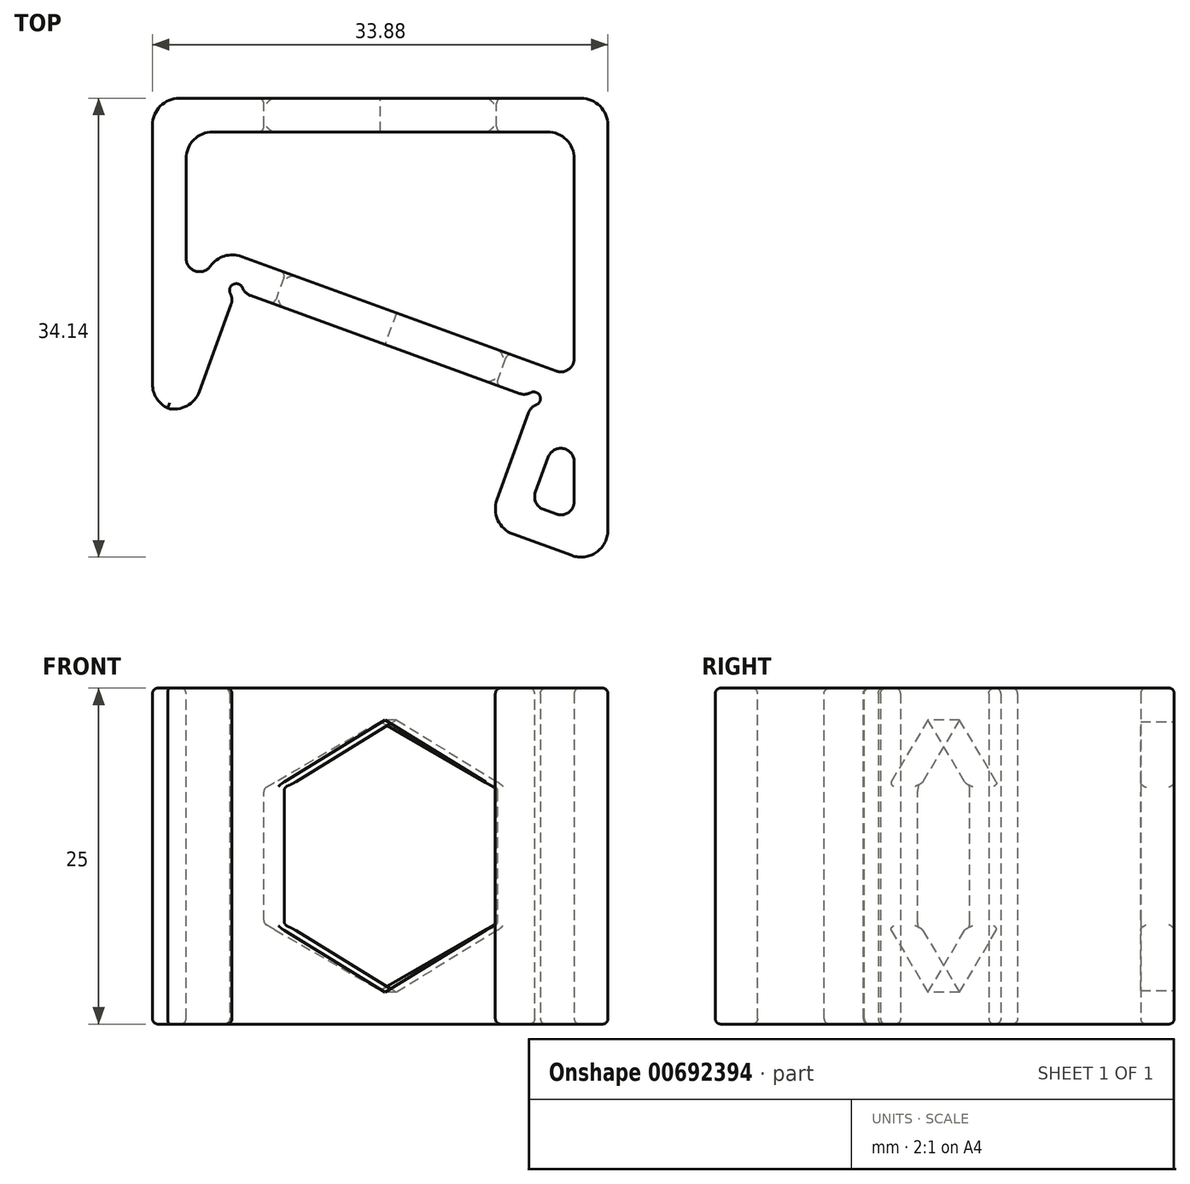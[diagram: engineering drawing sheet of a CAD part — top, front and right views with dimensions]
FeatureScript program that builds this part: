
annotation { "Feature Type Name" : "Feature", "Feature Type Description" : "" }
export const myFeature = defineFeature(function(context is Context, id is Id, definition is map)
    precondition{}
    {
        {
            var Q0;
            Q0=qCreatedBy(makeId("Right.planeOp"),FACE);
            var sketch = newSketch(context, id + "F0", { "sketchPlane" : qUnion([Q0])});
            skLineSegment(sketch, "E0", {"start": v(0, 0) * mm, "end": v(14.56, 0) * mm});
            skLineSegment(sketch, "E1", {"start": v(14.56, 0) * mm, "end": v(14.56, 40) * mm, "construction": true});
            skLineSegment(sketch, "E2", {"start": v(14.56, 40) * mm, "end": v(11.3, 31.06) * mm});
            skPoint(sketch, "E3", {"position": v(7.28, 20) * mm});
            skLineSegment(sketch, "E4", {"start": v(12.65, 5.51) * mm, "end": v(20.7, 27.64) * mm});
            skLineSegment(sketch, "E5", {"start": v(16.68, 16.58) * mm, "end": v(7.28, 20) * mm, "construction": true});
            skLineSegment(sketch, "E6", {"start": v(14.56, 0) * mm, "end": v(35, 0) * mm});
            skLineSegment(sketch, "E7", {"start": v(35, 0) * mm, "end": v(35, 40) * mm});
            skLineSegment(sketch, "E8", {"start": v(35, 40) * mm, "end": v(14.56, 40) * mm});
            skLineSegment(sketch, "E9", {"start": v(12.65, 5.51) * mm, "end": v(3.25, 8.94) * mm});
            skLineSegment(sketch, "E10", {"start": v(20.7, 27.64) * mm, "end": v(11.3, 31.06) * mm});
            skLineSegment(sketch, "E11", {"start": v(3.25, 8.94) * mm, "end": v(0, 0) * mm});
            skLineSegment(sketch, "E12", {"start": v(11.3, 31.06) * mm, "end": v(3.25, 8.94) * mm, "construction": true});
            skCircle(sketch, "E13", {"center": v(20.7, 27.64) * mm, "radius": 0.5 * mm});
            skCircle(sketch, "E14", {"center": v(12.65, 5.51) * mm, "radius": 0.5 * mm});
            skLineSegment(sketch, "E15", {"start": v(12.33, 33.88) * mm, "end": v(35, 33.88) * mm});
            skLineSegment(sketch, "E16.0", {"start": v(4.75, 5.73) * mm, "end": v(3.57, 2.5) * mm});
            skLineSegment(sketch, "E16.1", {"start": v(14.14, 2.31) * mm, "end": v(4.75, 5.73) * mm});
            skLineSegment(sketch, "E16.2", {"start": v(3.57, 2.5) * mm, "end": v(23.1, 2.5) * mm});
            skLineSegment(sketch, "E16.3", {"start": v(14.14, 2.31) * mm, "end": v(23.9, 29.14) * mm});
            skLineSegment(sketch, "E16.4", {"start": v(23.9, 29.14) * mm, "end": v(14.51, 32.56) * mm});
            skLineSegment(sketch, "E16.5", {"start": v(23.1, 2.5) * mm, "end": v(32.5, 2.5) * mm});
            skLineSegment(sketch, "E16.6", {"start": v(32.5, 2.5) * mm, "end": v(32.5, 37.5) * mm});
            skLineSegment(sketch, "E16.7", {"start": v(32.5, 37.5) * mm, "end": v(16.3, 37.5) * mm});
            skLineSegment(sketch, "E16.8", {"start": v(16.3, 37.5) * mm, "end": v(14.51, 32.56) * mm});
            skLineSegment(sketch, "E17", {"start": v(32.5, 31.38) * mm, "end": v(17.74, 31.38) * mm});
            skSolve(sketch);
        }
        {
            var Q0;
            Q0=makeQuery(id+"F0.imprint","IMPRINT",FACE,{"disambiguationData":[TD([[makeQuery(id+"F0.imprint","IMPRINT",EDGE,{"derivedFrom":sQuery(id+"F0.wireOp",EDGE,"E0")}),1.0]])]});
            var Q1;
            {var subQ0=sQuery(id+"F0.wireOp",EDGE,"E16.3");var subQ1=sQuery(id+"F0.wireOp",EDGE,"E16.1");var subQ2=makeQuery(id+"F0.imprint","INTERSECT",VERTEX,{"derivedFrom":[subQ1,subQ0]});Q1=makeQuery(id+"F0.imprint","IMPRINT",FACE,{"disambiguationData":[TD([[makeQuery(id+"F0.imprint","IMPRINT",EDGE,{"disambiguationData":[TD([[subQ2,-1.0]])],"derivedFrom":subQ1}),-1.0]])]});}
            var Q2;
            {var subQ5=sQuery(id+"F0.wireOp",EDGE,"E17");Q2=makeQuery(id+"F0.imprint","IMPRINT",FACE,{"disambiguationData":[TD([[makeQuery(id+"F0.imprint","IMPRINT",EDGE,{"derivedFrom":subQ5}),-1.0]])]});}
            extrude(context, id + "F1", {"entities" : qUnion([Q0, Q1, Q2]), "depth" : 25 * mm, "offsetDistance" : 25 * mm});
        }
        {
            var Q0;
            Q0=makeQuery(id+"F1.opExtrude","SWEPT_FACE",FACE,{"disambiguationData":[OSD([sQuery(id+"F0.wireOp",EDGE,"E4")])]});
            var sketch = newSketch(context, id + "F2", { "sketchPlane" : qUnion([Q0])});
            skPoint(sketch, "E18.0", {"position": v(12.5, 32.56) * mm});
            skPoint(sketch, "E18.1", {"position": v(0, 21.28) * mm});
            skLineSegment(sketch, "E19", {"start": v(0, 21.28) * mm, "end": v(22.76, 21.28) * mm, "construction": true});
            skLineSegment(sketch, "E20", {"start": v(12.5, 32.56) * mm, "end": v(12.5, 21.28) * mm, "construction": true});
            skCircle(sketch, "E21.cCircle", {"center": v(12.5, 21.28) * mm, "radius": 8.78 * mm, "construction": true});
            skLineSegment(sketch, "E21.0", {"start": v(7.43, 30.06) * mm, "end": v(17.57, 30.06) * mm});
            skLineSegment(sketch, "E21.1", {"start": v(17.57, 30.06) * mm, "end": v(22.63, 21.28) * mm});
            skLineSegment(sketch, "E21.2", {"start": v(22.63, 21.28) * mm, "end": v(17.57, 12.5) * mm});
            skLineSegment(sketch, "E21.3", {"start": v(17.57, 12.5) * mm, "end": v(7.43, 12.5) * mm});
            skLineSegment(sketch, "E21.4", {"start": v(7.43, 12.5) * mm, "end": v(2.37, 21.28) * mm});
            skLineSegment(sketch, "E21.5", {"start": v(2.37, 21.28) * mm, "end": v(7.43, 30.06) * mm});
            skPoint(sketch, "E21.0.midPoint", {"position": v(12.5, 30.06) * mm});
            skSolve(sketch);
        }
        {
            var Q0;
            Q0=makeQuery(id+"F2.imprint","IMPRINT",FACE,{"disambiguationData":[TD([[makeQuery(id+"F2.imprint","IMPRINT",EDGE,{"derivedFrom":sQuery(id+"F2.wireOp",EDGE,"E21.0")}),-1.0]])]});
            extrude(context, id + "F3", {"entities" : qUnion([Q0]), "operationType" : NewBodyOperationType.REMOVE, "oppositeDirection" : true, "depth" : 4.6 * mm, "offsetDistance" : 25 * mm});
        }
        {
            var Q0;
            Q0=makeQuery(id+"F1.opExtrude","SWEPT_FACE",FACE,{"disambiguationData":[OSD([sQuery(id+"F0.wireOp",EDGE,"E7")])]});
            var sketch = newSketch(context, id + "F4", { "sketchPlane" : qUnion([Q0])});
            skPoint(sketch, "E22.0", {"position": v(-12.5, 33.88) * mm});
            skPoint(sketch, "E22.1", {"position": v(-25, 16.94) * mm});
            skLineSegment(sketch, "E23", {"start": v(-25, 16.94) * mm, "end": v(-8.51, 16.94) * mm, "construction": true});
            skLineSegment(sketch, "E24", {"start": v(-12.5, 33.88) * mm, "end": v(-12.5, 16.94) * mm, "construction": true});
            skCircle(sketch, "E25.cCircle", {"center": v(-12.5, 16.94) * mm, "radius": 8.66 * mm, "construction": true});
            skLineSegment(sketch, "E25.0", {"start": v(-17.5, 25.6) * mm, "end": v(-7.5, 25.6) * mm});
            skLineSegment(sketch, "E25.1", {"start": v(-7.5, 25.6) * mm, "end": v(-2.5, 16.94) * mm});
            skLineSegment(sketch, "E25.2", {"start": v(-2.5, 16.94) * mm, "end": v(-7.5, 8.28) * mm});
            skLineSegment(sketch, "E25.3", {"start": v(-7.5, 8.28) * mm, "end": v(-17.5, 8.28) * mm});
            skLineSegment(sketch, "E25.4", {"start": v(-17.5, 8.28) * mm, "end": v(-22.5, 16.94) * mm});
            skLineSegment(sketch, "E25.5", {"start": v(-22.5, 16.94) * mm, "end": v(-17.5, 25.6) * mm});
            skPoint(sketch, "E25.0.midPoint", {"position": v(-12.5, 25.6) * mm});
            skSolve(sketch);
        }
        {
            var Q0;
            Q0=makeQuery(id+"F4.imprint","IMPRINT",FACE,{"disambiguationData":[TD([[makeQuery(id+"F4.imprint","IMPRINT",EDGE,{"derivedFrom":sQuery(id+"F4.wireOp",EDGE,"E25.0")}),-1.0]])]});
            extrude(context, id + "F5", {"entities" : qUnion([Q0]), "operationType" : NewBodyOperationType.REMOVE, "oppositeDirection" : true, "depth" : 4.8 * mm, "offsetDistance" : 25 * mm});
        }
        {
            var Q0;
            Q0=makeQuery(id+"F1.opExtrude","SWEPT_EDGE",EDGE,{"disambiguationData":[OSD([sQuery(id+"F0.wireOp",EDGE,"E9"),sQuery(id+"F0.wireOp",EDGE,"E11")])]});
            var Q1;
            Q1=makeQuery(id+"F1.opExtrude","SWEPT_EDGE",EDGE,{"disambiguationData":[OSD([sQuery(id+"F0.wireOp",EDGE,"E2"),sQuery(id+"F0.wireOp",EDGE,"E10")])]});
            var Q2;
            Q2=makeQuery(id+"F1.opExtrude","SWEPT_EDGE",EDGE,{"disambiguationData":[OSD([sQuery(id+"F0.wireOp",EDGE,"E2"),sQuery(id+"F0.wireOp",EDGE,"E8")])]});
            var Q3;
            Q3=makeQuery(id+"F1.opExtrude","SWEPT_EDGE",EDGE,{"disambiguationData":[OSD([sQuery(id+"F0.wireOp",EDGE,"E7"),sQuery(id+"F0.wireOp",EDGE,"E8")])]});
            var Q4;
            Q4=makeQuery(id+"F1.opExtrude","SWEPT_EDGE",EDGE,{"disambiguationData":[OSD([sQuery(id+"F0.wireOp",EDGE,"E0"),sQuery(id+"F0.wireOp",EDGE,"E11")])]});
            var Q5;
            Q5=makeQuery(id+"F1.opExtrude","SWEPT_EDGE",EDGE,{"disambiguationData":[OSD([sQuery(id+"F0.wireOp",EDGE,"E6"),sQuery(id+"F0.wireOp",EDGE,"E7")])]});
            var Q6;
            Q6=makeQuery(id+"F1.opExtrude","SWEPT_EDGE",EDGE,{"disambiguationData":[OSD([sQuery(id+"F0.wireOp",EDGE,"E16.6"),sQuery(id+"F0.wireOp",EDGE,"E17")])]});
            var Q7;
            Q7=makeQuery(id+"F1.opExtrude","SWEPT_EDGE",EDGE,{"disambiguationData":[OSD([sQuery(id+"F0.wireOp",EDGE,"E16.5"),sQuery(id+"F0.wireOp",EDGE,"E16.6")])]});
            var Q8;
            Q8=makeQuery(id+"F1.opExtrude","SWEPT_EDGE",EDGE,{"disambiguationData":[OSD([sQuery(id+"F0.wireOp",EDGE,"E16.3"),sQuery(id+"F0.wireOp",EDGE,"E16.4")])]});
            fillet(context, id + "F6", {"entities" : qUnion([Q0, Q1, Q2, Q3, Q4, Q5, Q6, Q7, Q8]), "radius" : 2 * mm, "tangentPropagation" : true, "allowEdgeOverflow" : false});
        }
        {
            var Q0;
            Q0=makeQuery(id+"F1.opExtrude","SWEPT_EDGE",EDGE,{"disambiguationData":[OSD([sQuery(id+"F0.wireOp",EDGE,"E4"),sQuery(id+"F0.wireOp",EDGE,"E13")])]});
            var Q1;
            Q1=makeQuery(id+"F1.opExtrude","SWEPT_EDGE",EDGE,{"disambiguationData":[OSD([sQuery(id+"F0.wireOp",EDGE,"E10"),sQuery(id+"F0.wireOp",EDGE,"E13")])]});
            var Q2;
            Q2=makeQuery(id+"F1.opExtrude","SWEPT_EDGE",EDGE,{"disambiguationData":[OSD([sQuery(id+"F0.wireOp",EDGE,"E9"),sQuery(id+"F0.wireOp",EDGE,"E14")])]});
            var Q3;
            Q3=makeQuery(id+"F1.opExtrude","SWEPT_EDGE",EDGE,{"disambiguationData":[OSD([sQuery(id+"F0.wireOp",EDGE,"E4"),sQuery(id+"F0.wireOp",EDGE,"E14")])]});
            var Q4;
            Q4=makeQuery(id+"F1.opExtrude","SWEPT_EDGE",EDGE,{"disambiguationData":[OSD([sQuery(id+"F0.wireOp",EDGE,"E16.2"),sQuery(id+"F0.wireOp",EDGE,"E16.3")])]});
            var Q5;
            Q5=makeQuery(id+"F1.opExtrude","SWEPT_EDGE",EDGE,{"disambiguationData":[OSD([sQuery(id+"F0.wireOp",EDGE,"E16.4"),sQuery(id+"F0.wireOp",EDGE,"E17")])]});
            var Q6;
            Q6=makeQuery(id+"F1.opExtrude","SWEPT_EDGE",EDGE,{"disambiguationData":[OSD([sQuery(id+"F0.wireOp",EDGE,"E16.0"),sQuery(id+"F0.wireOp",EDGE,"E16.1")])]});
            var Q7;
            Q7=makeQuery(id+"F1.opExtrude","SWEPT_EDGE",EDGE,{"disambiguationData":[OSD([sQuery(id+"F0.wireOp",EDGE,"E16.1"),sQuery(id+"F0.wireOp",EDGE,"E16.2")])]});
            var Q8;
            Q8=makeQuery(id+"F1.opExtrude","SWEPT_EDGE",EDGE,{"disambiguationData":[OSD([sQuery(id+"F0.wireOp",EDGE,"E16.0"),sQuery(id+"F0.wireOp",EDGE,"E16.2")])]});
            fillet(context, id + "F7", {"entities" : qUnion([Q0, Q1, Q2, Q3, Q4, Q5, Q6, Q7, Q8]), "radius" : 1 * mm, "tangentPropagation" : true, "allowEdgeOverflow" : false});
        }
        {
            var Q0;
            Q0=makeQuery(id+"F1.opExtrude","CAP_EDGE",EDGE,{"disambiguationData":[OSD([sQuery(id+"F0.wireOp",EDGE,"E4")])],"isStart":false});
            var Q1;
            Q1=makeQuery(id+"F1.opExtrude","CAP_EDGE",EDGE,{"disambiguationData":[OSD([sQuery(id+"F0.wireOp",EDGE,"E4")])],"isStart":true});
            var Q2;
            Q2=makeQuery(id+"F1.opExtrude","CAP_EDGE",EDGE,{"disambiguationData":[OSD([sQuery(id+"F0.wireOp",EDGE,"E16.3")])],"isStart":false});
            var Q3;
            Q3=makeQuery(id+"F1.opExtrude","CAP_EDGE",EDGE,{"disambiguationData":[OSD([sQuery(id+"F0.wireOp",EDGE,"E16.0")])],"isStart":false});
            var Q4;
            Q4=makeQuery(id+"F1.opExtrude","CAP_EDGE",EDGE,{"disambiguationData":[OSD([sQuery(id+"F0.wireOp",EDGE,"E16.3")])],"isStart":true});
            var Q5;
            Q5=makeQuery(id+"F1.opExtrude","CAP_EDGE",EDGE,{"disambiguationData":[OSD([sQuery(id+"F0.wireOp",EDGE,"E16.1")])],"isStart":true});
            var Q6;
            Q6=makeQuery(id+"F3.boolean.opBoolean","COPY",FACE,{"derivedFrom":makeQuery(id+"F3.opExtrude","SWEPT_FACE",FACE,{"disambiguationData":[OSD([sQuery(id+"F2.wireOp",EDGE,"E21.3")])]})});
            var Q7;
            Q7=makeQuery(id+"F5.boolean.opBoolean","COPY",FACE,{"derivedFrom":makeQuery(id+"F5.opExtrude","SWEPT_FACE",FACE,{"disambiguationData":[OSD([sQuery(id+"F4.wireOp",EDGE,"E25.3")])]})});
            var Q8;
            Q8=makeQuery(id+"F5.boolean.opBoolean","COPY",FACE,{"derivedFrom":makeQuery(id+"F5.opExtrude","SWEPT_FACE",FACE,{"disambiguationData":[OSD([sQuery(id+"F4.wireOp",EDGE,"E25.0")])]})});
            var Q9;
            Q9=makeQuery(id+"F3.boolean.opBoolean","COPY",FACE,{"derivedFrom":makeQuery(id+"F3.opExtrude","SWEPT_FACE",FACE,{"disambiguationData":[OSD([sQuery(id+"F2.wireOp",EDGE,"E21.0")])]})});
            fillet(context, id + "F8", {"entities" : qUnion([Q0, Q1, Q2, Q3, Q4, Q5, Q6, Q7, Q8, Q9]), "radius" : 0.4 * mm, "tangentPropagation" : true, "allowEdgeOverflow" : false});
        }
        {
            var Q0;
            Q0=makeQuery(id+"F1.opExtrude","SWEPT_BODY",BODY,{"disambiguationData":[OSD([sQuery(id+"F0.wireOp",EDGE,"E0"),sQuery(id+"F0.wireOp",EDGE,"E2"),sQuery(id+"F0.wireOp",EDGE,"E4"),sQuery(id+"F0.wireOp",EDGE,"E6"),sQuery(id+"F0.wireOp",EDGE,"E7"),sQuery(id+"F0.wireOp",EDGE,"E9"),sQuery(id+"F0.wireOp",EDGE,"E10"),sQuery(id+"F0.wireOp",EDGE,"E11"),sQuery(id+"F0.wireOp",EDGE,"E13"),sQuery(id+"F0.wireOp",EDGE,"E14"),sQuery(id+"F0.wireOp",EDGE,"E15"),sQuery(id+"F0.wireOp",EDGE,"E16.0"),sQuery(id+"F0.wireOp",EDGE,"E16.1"),sQuery(id+"F0.wireOp",EDGE,"E16.2"),sQuery(id+"F0.wireOp",EDGE,"E16.3"),sQuery(id+"F0.wireOp",EDGE,"E16.4"),sQuery(id+"F0.wireOp",EDGE,"E16.5"),sQuery(id+"F0.wireOp",EDGE,"E16.6"),sQuery(id+"F0.wireOp",EDGE,"E17")])]});
            var Q1;
            {var subQ0=sQuery(id+"F0.wireOp",EDGE,"E6");var subQ1=sQuery(id+"F0.wireOp",EDGE,"E0");Q1=makeQuery(id+"F8.opFillet","BLEND_EDGE",EDGE,{"blendedFrom":[makeQuery(id+"F1.opExtrude","CAP_EDGE",EDGE,{"disambiguationData":[OSD([subQ1,subQ0])],"isStart":true}),makeQuery(id+"F1.opExtrude","SWEPT_FACE",FACE,{"disambiguationData":[OSD([subQ1,subQ0])]})],"blendedInto":[makeQuery(id+"F1.opExtrude","SWEPT_FACE",FACE,{"disambiguationData":[OSD([subQ1,subQ0])]})]});}
            transform(context, id + "F9", {"entities" : qUnion([Q0]), "transformType" : TransformType.ROTATION, "transformAxis" : qUnion([Q1]), "angle" : 90 * degree, "oppositeDirection" : true, "makeCopy" : false});
        }
    });
